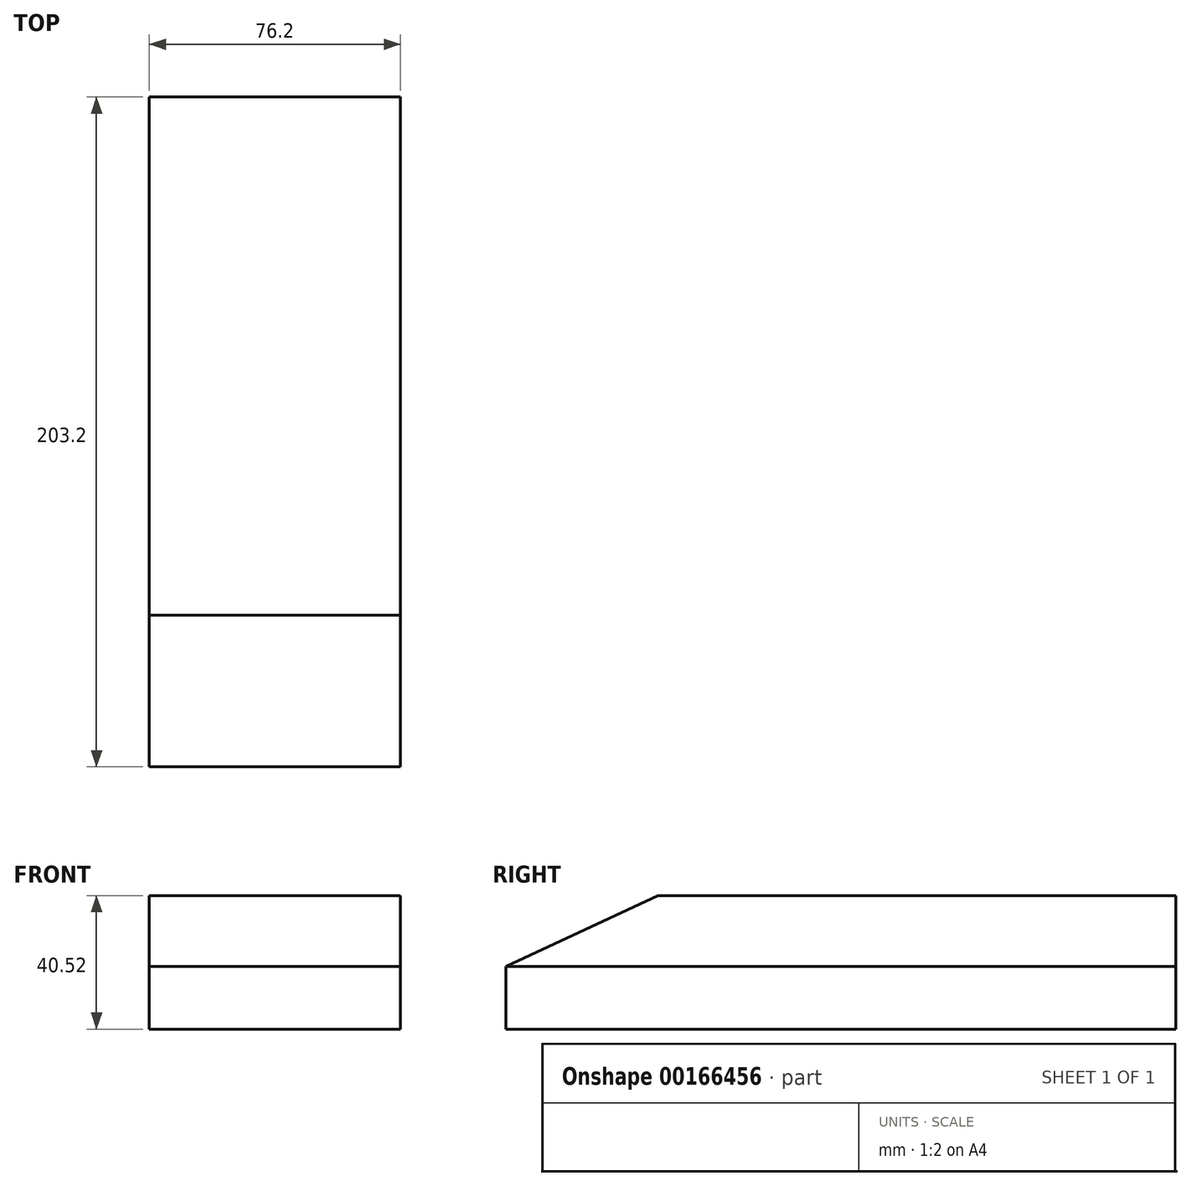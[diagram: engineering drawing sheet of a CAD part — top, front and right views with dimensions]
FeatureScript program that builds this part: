
annotation { "Feature Type Name" : "Feature", "Feature Type Description" : "" }
export const myFeature = defineFeature(function(context is Context, id is Id, definition is map)
    precondition{}
    {
        {
            var Q0;
            Q0=qCreatedBy(makeId("Right.planeOp"),FACE);
            var sketch = newSketch(context, id + "F0", { "sketchPlane" : qUnion([Q0])});
            skLineSegment(sketch, "E0", {"start": v(0, 0) * mm, "end": v(46.04, 21.47) * mm});
            skLineSegment(sketch, "E1", {"start": v(46.04, 21.47) * mm, "end": v(203.2, 21.47) * mm});
            skLineSegment(sketch, "E2", {"start": v(203.2, 21.47) * mm, "end": v(203.2, 0) * mm});
            skLineSegment(sketch, "E3", {"start": v(203.2, 0) * mm, "end": v(0, 0) * mm});
            skSolve(sketch);
        }
        {
            var Q0;
            Q0=makeQuery(id+"F0.imprint","IMPRINT",FACE,{"disambiguationData":[TD([[makeQuery(id+"F0.imprint","IMPRINT",EDGE,{"derivedFrom":sQuery(id+"F0.wireOp",EDGE,"E0")}),-1.0]])]});
            extrude(context, id + "F1", {"entities" : qUnion([Q0]), "endBound" : BoundingType.SYMMETRIC, "depth" : 76.2 * mm});
        }
        {
            var Q0;
            Q0=qCreatedBy(makeId("Right.planeOp"),FACE);
            var sketch = newSketch(context, id + "F2", { "sketchPlane" : qUnion([Q0])});
            skLineSegment(sketch, "E4.bottom", {"start": v(0, 0) * mm, "end": v(203.2, 0) * mm});
            skLineSegment(sketch, "E4.top", {"start": v(0, -19.05) * mm, "end": v(203.2, -19.05) * mm});
            skLineSegment(sketch, "E4.left", {"start": v(0, 0) * mm, "end": v(0, -19.05) * mm});
            skLineSegment(sketch, "E4.right", {"start": v(203.2, 0) * mm, "end": v(203.2, -19.05) * mm});
            skSolve(sketch);
        }
        {
            var Q0;
            Q0 = qSketchRegion(id + "F2", true);
            extrude(context, id + "F3", {"entities" : qUnion([Q0]), "endBound" : BoundingType.SYMMETRIC, "depth" : 76.2 * mm});
        }
    });
